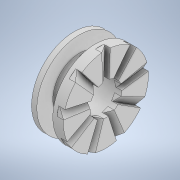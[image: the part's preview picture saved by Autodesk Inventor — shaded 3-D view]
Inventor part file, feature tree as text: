
AUTODESK INVENTOR PART (.ipt)
format: ipt  version: 2021 (Build 250183000, 183)  size: 313,856 bytes
history: native  units: in
note: dims shown in document units (in); Inventor stores cm internally (conversion verified against a paired STEP export)
features: sketch x7, plane x3, hole x2, pattern_circular x2, revolve x1, extrude x1, loft x1, other x1
ambient origin geometry x8: Origin, YZ Plane, XZ Plane, XY Plane, X Axis, Y Axis, Z Axis, Center Point
bodies: Solid1 (feature_tree)
feature tree (18):
  revolve  "Revolution1"  [1 undecoded]
  hole  "Hole1"  [1 undecoded]
  plane  "Work Plane1"
  plane  "Work Plane2"
  sketch  "Sketch3"  dims[d4=3.1496in d5=3.1496in d6=1.9685in]
  extrude  "Extrusion1"  Depth=3.1496in
  pattern_circular  "Circular Pattern2"  Count=5  [1 undecoded]
  sketch  "Sketch7"  dims[d10=1.1811in d11=0.2362in d12=0.1575in d13=0.0787in d14=90.0deg d15=0.5906in d16=0.0in d17=0.1575in d18=-0.1575in]
  loft  "Loft2"
  pattern_circular  "Circular Pattern3"  Count=3  [1 undecoded]
  plane  "Work Plane3"
  hole  "Hole2"  [1 undecoded]
  sketch  "Sketch1"  dims[d0=0.5906in d1=0.1575in]
  sketch  "Sketch2"  dims[d2=0.1969in d3=0.5906in]
  sketch  "Sketch6"  dims[d7=90.0deg d8=1.1811in d9=1.1811in]
  sketch  "Sketch8"  dims[d30=0.315in]
  other  "Edges1"
  sketch  "Sketch9"  dims[d31=0.1575in d32=0.2362in d33=0.1181in d34=3.5433in d36=360.0deg d38=0.2362in d39=0.0in d40=3.5433in d41=360.0deg d46=0.0394in d47=0.9843in d48=0.0in d49=90.0deg d50=0.0in d51=90.0deg d52=3.5433in d53=360.0deg d55=0.9843in d56=0.3937in d57=0.4331in d58=0.2362in d59=0.7874in d60=0.0787in d61=90.0deg d62=0.5025in d63=0.0in]
note: 5 required parameter values undecoded (feature->parameter linkage not recoverable at this tier; creation-order binding heuristic only, values carry confidence <= 0.55)